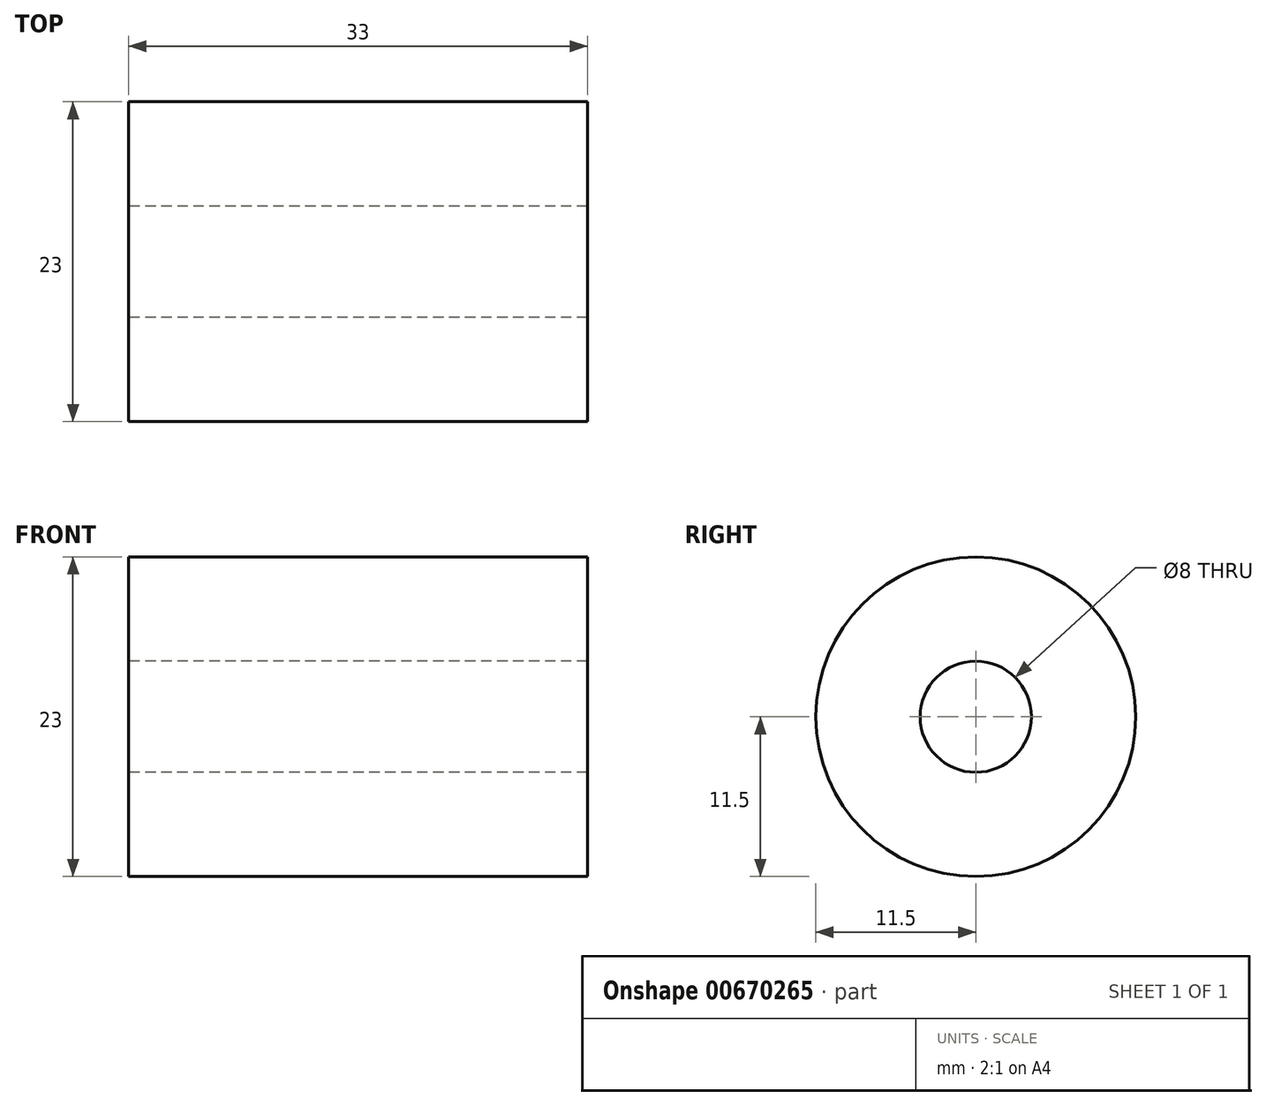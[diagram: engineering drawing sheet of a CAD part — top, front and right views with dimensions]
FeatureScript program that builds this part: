
annotation { "Feature Type Name" : "Feature", "Feature Type Description" : "" }
export const myFeature = defineFeature(function(context is Context, id is Id, definition is map)
    precondition{}
    {
        {
            var Q0;
            Q0=qCreatedBy(makeId("Right.planeOp"),FACE);
            var sketch = newSketch(context, id + "F0", { "sketchPlane" : qUnion([Q0])});
            skCircle(sketch, "E0", {"center": v(0, 0) * mm, "radius": 11.5 * mm});
            skCircle(sketch, "E1", {"center": v(0, 0) * mm, "radius": 4 * mm});
            skSolve(sketch);
        }
        {
            var Q0;
            Q0=makeQuery(id+"F0.imprint","IMPRINT",FACE,{"disambiguationData":[TD([[makeQuery(id+"F0.imprint","IMPRINT",EDGE,{"derivedFrom":sQuery(id+"F0.wireOp",EDGE,"E0")}),1.0]])]});
            extrude(context, id + "F1", {"entities" : qUnion([Q0]), "depth" : 33 * mm, "offsetDistance" : 25 * mm});
        }
    });
